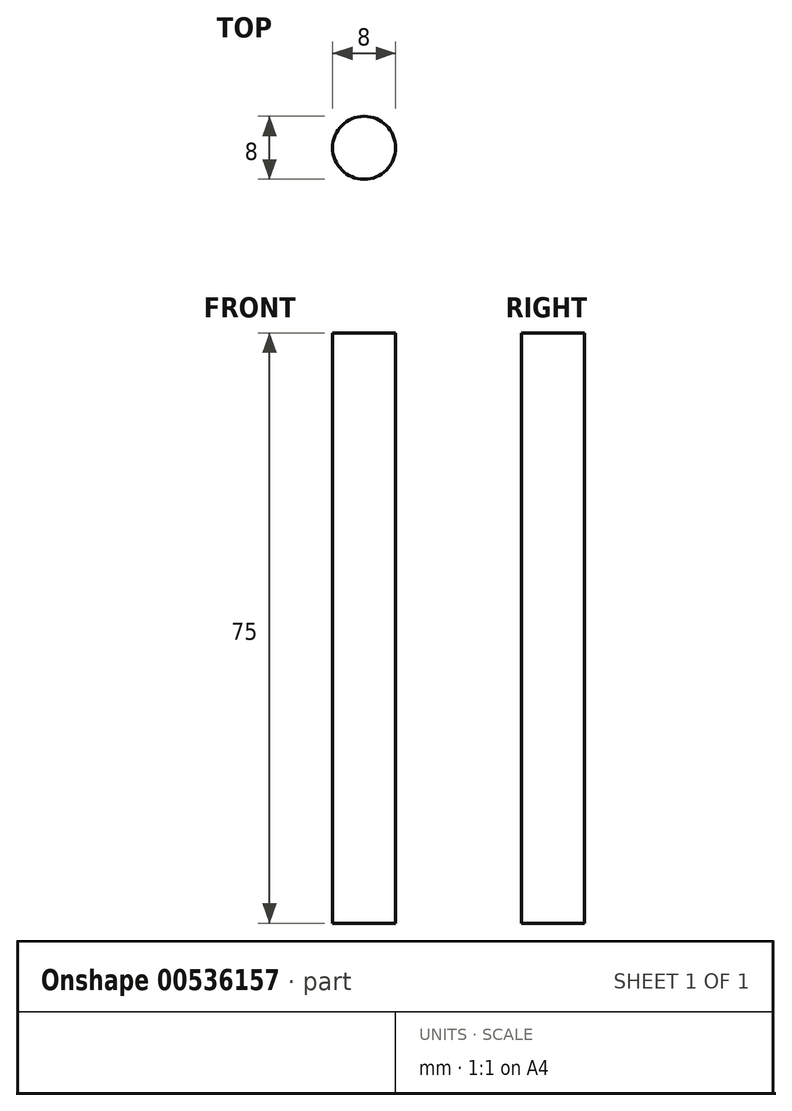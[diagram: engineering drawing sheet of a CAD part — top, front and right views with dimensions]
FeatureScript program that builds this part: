
annotation { "Feature Type Name" : "Feature", "Feature Type Description" : "" }
export const myFeature = defineFeature(function(context is Context, id is Id, definition is map)
    precondition{}
    {
        {
            var Q0;
            Q0=qCreatedBy(makeId("Top.planeOp"),FACE);
            var sketch = newSketch(context, id + "F0", { "sketchPlane" : qUnion([Q0])});
            skCircle(sketch, "E0", {"center": v(0, 0) * mm, "radius": 4 * mm});
            skSolve(sketch);
        }
        {
            var Q0;
            Q0 = qSketchRegion(id + "F0", true);
            extrude(context, id + "F1", {"entities" : qUnion([Q0]), "depth" : 75 * mm, "offsetDistance" : 25 * mm});
        }
    });
